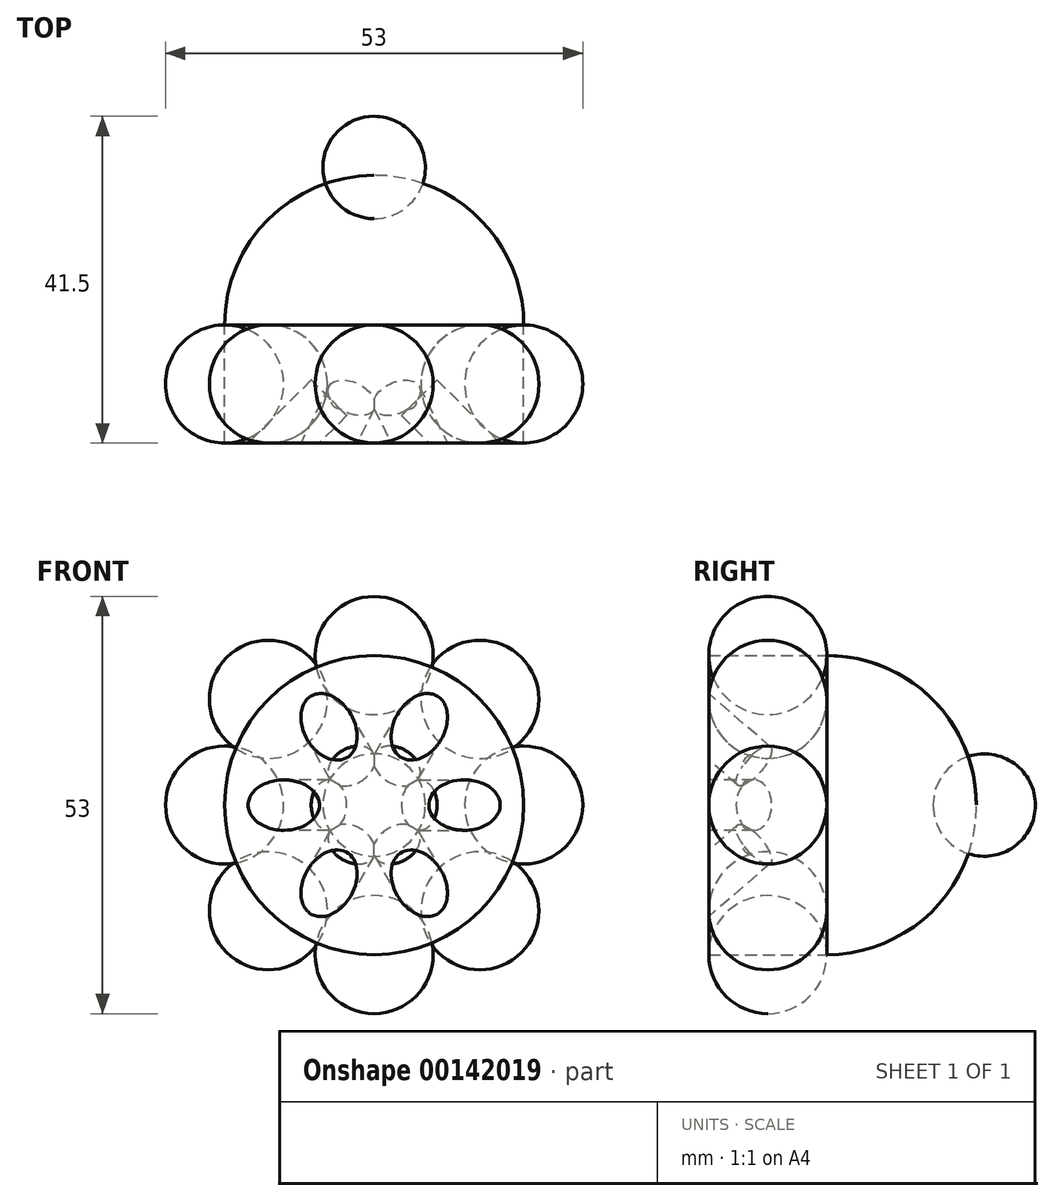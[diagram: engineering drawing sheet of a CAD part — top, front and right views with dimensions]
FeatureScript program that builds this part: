
annotation { "Feature Type Name" : "Feature", "Feature Type Description" : "" }
export const myFeature = defineFeature(function(context is Context, id is Id, definition is map)
    precondition{}
    {
        {
            var Q0;
            Q0=qCreatedBy(makeId("Front.planeOp"),FACE);
            var sketch = newSketch(context, id + "F0", { "sketchPlane" : qUnion([Q0])});
            skArc(sketch, "E0", {"start": v(7.5, 19) * mm, "mid": v(0, 26.5) * mm, "end": v(-7.5, 19) * mm});
            skLineSegment(sketch, "E1", {"start": v(-7.5, 19) * mm, "end": v(7.5, 19) * mm});
            skLineSegment(sketch, "E2", {"start": v(0, 19) * mm, "end": v(0, 0) * mm});
            skSolve(sketch);
        }
        {
            var Q0;
            Q0 = qSketchRegion(id + "F0", true);
            var Q1;
            Q1=sQuery(id+"F0.wireOp",EDGE,"E1");
            revolve(context, id + "F1", {"entities" : qUnion([Q0]), "axis" : qUnion([Q1]), "revolveType" : RevolveType.FULL});
        }
        {
            var Q0;
            Q0=qCreatedBy(makeId("Top.planeOp"),FACE);
            var sketch = newSketch(context, id + "F2", { "sketchPlane" : qUnion([Q0])});
            skLineSegment(sketch, "E3", {"start": v(0, 71.79) * mm, "end": v(0, -73.96) * mm});
            skSolve(sketch);
        }
        {
            var Q0;
            Q0=makeQuery(id+"F1.opRevolve","SWEPT_BODY",BODY,{"disambiguationData":[OSD([sQuery(id+"F0.wireOp",EDGE,"E0"),sQuery(id+"F0.wireOp",EDGE,"E1")])]});
            var Q1;
            Q1=sQuery(id+"F2.wireOp",EDGE,"E3");
            circularPattern(context, id + "F3", {"entities" : qUnion([Q0]), "axis" : qUnion([Q1]), "angle" : 45 * degree, "instanceCount" : 8});
        }
        {
            var Q0;
            Q0=qCreatedBy(makeId("Front.planeOp"),FACE);
            var sketch = newSketch(context, id + "F4", { "sketchPlane" : qUnion([Q0])});
            skCircle(sketch, "E4", {"center": v(0, 0) * mm, "radius": 19 * mm});
            skSolve(sketch);
        }
        {
            var Q0;
            Q0 = qSketchRegion(id + "F4", true);
            extrude(context, id + "F5", {"entities" : qUnion([Q0]), "endBound" : BoundingType.SYMMETRIC, "depth" : 15 * mm, "hasSecondDirection" : true, "secondDirectionOppositeDirection" : true, "secondDirectionDepth" : 25 * mm});
        }
        {
            var Q0;
            Q0=qCreatedBy(makeId("Right.planeOp"),FACE);
            var sketch = newSketch(context, id + "F6", { "sketchPlane" : qUnion([Q0])});
            skArc(sketch, "E5", {"start": v(26.5, 0) * mm, "mid": v(20.94, 13.44) * mm, "end": v(7.5, 19) * mm});
            skLineSegment(sketch, "E6", {"start": v(7.5, 19) * mm, "end": v(7.5, 0) * mm});
            skLineSegment(sketch, "E7", {"start": v(26.5, 0) * mm, "end": v(7.5, 0) * mm});
            skSolve(sketch);
        }
        {
            var Q0;
            Q0=qCreatedBy(makeId("Right.planeOp"),FACE);
            var sketch = newSketch(context, id + "F7", { "sketchPlane" : qUnion([Q0])});
            skLineSegment(sketch, "E8", {"start": v(118.27, 0) * mm, "end": v(-121.95, 0) * mm, "construction": true});
            skSolve(sketch);
        }
        {
            var Q0;
            Q0 = qSketchRegion(id + "F6", true);
            var Q1;
            Q1=sQuery(id+"F7.wireOp",EDGE,"E8");
            revolve(context, id + "F8", {"entities" : qUnion([Q0]), "axis" : qUnion([Q1]), "revolveType" : RevolveType.FULL});
        }
        {
            var Q0;
            Q0=qCreatedBy(makeId("Right.planeOp"),FACE);
            var sketch = newSketch(context, id + "F9", { "sketchPlane" : qUnion([Q0])});
            skArc(sketch, "E9", {"start": v(34, 0) * mm, "mid": v(27.5, 6.5) * mm, "end": v(21, 0) * mm});
            skLineSegment(sketch, "E10", {"start": v(34, 0) * mm, "end": v(21, 0) * mm});
            skSolve(sketch);
        }
        {
            var Q0;
            Q0=makeQuery(id+"F9.imprint","IMPRINT",FACE,{"disambiguationData":[TD([[makeQuery(id+"F9.imprint","IMPRINT",EDGE,{"derivedFrom":sQuery(id+"F9.wireOp",EDGE,"E9")}),1.0]])]});
            var Q1;
            Q1=sQuery(id+"F9.wireOp",EDGE,"E9");
            var Q2;
            Q2=sQuery(id+"F7.wireOp",EDGE,"E8");
            revolve(context, id + "F10", {"entities" : qUnion([Q0]), "surfaceEntities" : qUnion([Q1]), "axis" : qUnion([Q2]), "revolveType" : RevolveType.FULL});
        }
        {
            var Q0;
            Q0=qCreatedBy(makeId("Top.planeOp"),FACE);
            var sketch = newSketch(context, id + "F11", { "sketchPlane" : qUnion([Q0])});
            skLineSegment(sketch, "E11", {"start": v(-16, -7.5) * mm, "end": v(-8, 0.5) * mm});
            skLineSegment(sketch, "E12", {"start": v(0, -7.5) * mm, "end": v(-143.96, 136.46) * mm, "construction": true});
            skLineSegment(sketch, "E13", {"start": v(-65.01, -61.04) * mm, "end": v(127.86, 131.84) * mm, "construction": true});
            skLineSegment(sketch, "E14", {"start": v(-8, 0.5) * mm, "end": v(-5.74, -1.76) * mm});
            skLineSegment(sketch, "E15", {"start": v(-5.74, -1.76) * mm, "end": v(-11.47, -7.5) * mm});
            skLineSegment(sketch, "E16", {"start": v(-11.47, -7.5) * mm, "end": v(-16, -7.5) * mm});
            skSolve(sketch);
        }
        {
            var Q0;
            Q0 = qSketchRegion(id + "F11", true);
            var Q1;
            Q1=sQuery(id+"F11.wireOp",EDGE,"E13");
            revolve(context, id + "F12", {"entities" : qUnion([Q0]), "axis" : qUnion([Q1]), "revolveType" : RevolveType.FULL});
        }
        {
            var Q0;
            Q0=makeQuery(id+"F12.opRevolve","SWEPT_BODY",BODY,{"disambiguationData":[OSD([sQuery(id+"F11.wireOp",EDGE,"E11"),sQuery(id+"F11.wireOp",EDGE,"E15"),sQuery(id+"F11.wireOp",EDGE,"E16"),sQuery(id+"F11.wireOp",EDGE,"HOoqhNjA-D5fc-TMDI-aKYZ-cZDTuwgksI9U")])]});
            var Q1;
            Q1=sQuery(id+"F7.wireOp",EDGE,"E8");
            circularPattern(context, id + "F13", {"entities" : qUnion([Q0]), "axis" : qUnion([Q1]), "angle" : 60 * degree, "instanceCount" : 6});
        }
        {
            var Q0;
            Q0=makeQuery(id+"F13.opPattern","COPY",BODY,{"derivedFrom":makeQuery(id+"F12.opRevolve","SWEPT_BODY",BODY,{"disambiguationData":[OSD([sQuery(id+"F11.wireOp",EDGE,"E11"),sQuery(id+"F11.wireOp",EDGE,"E15"),sQuery(id+"F11.wireOp",EDGE,"E16"),sQuery(id+"F11.wireOp",EDGE,"HOoqhNjA-D5fc-TMDI-aKYZ-cZDTuwgksI9U")])]}),"instanceName":"3"});
            var Q1;
            Q1=makeQuery(id+"F12.opRevolve","SWEPT_BODY",BODY,{"disambiguationData":[OSD([sQuery(id+"F11.wireOp",EDGE,"E11"),sQuery(id+"F11.wireOp",EDGE,"E15"),sQuery(id+"F11.wireOp",EDGE,"E16"),sQuery(id+"F11.wireOp",EDGE,"HOoqhNjA-D5fc-TMDI-aKYZ-cZDTuwgksI9U")])]});
            var Q2;
            Q2=makeQuery(id+"F13.opPattern","COPY",BODY,{"derivedFrom":makeQuery(id+"F12.opRevolve","SWEPT_BODY",BODY,{"disambiguationData":[OSD([sQuery(id+"F11.wireOp",EDGE,"E11"),sQuery(id+"F11.wireOp",EDGE,"E15"),sQuery(id+"F11.wireOp",EDGE,"E16"),sQuery(id+"F11.wireOp",EDGE,"HOoqhNjA-D5fc-TMDI-aKYZ-cZDTuwgksI9U")])]}),"instanceName":"1"});
            var Q3;
            Q3=makeQuery(id+"F13.opPattern","COPY",BODY,{"derivedFrom":makeQuery(id+"F12.opRevolve","SWEPT_BODY",BODY,{"disambiguationData":[OSD([sQuery(id+"F11.wireOp",EDGE,"E11"),sQuery(id+"F11.wireOp",EDGE,"E15"),sQuery(id+"F11.wireOp",EDGE,"E16"),sQuery(id+"F11.wireOp",EDGE,"HOoqhNjA-D5fc-TMDI-aKYZ-cZDTuwgksI9U")])]}),"instanceName":"2"});
            var Q4;
            Q4=makeQuery(id+"F13.opPattern","COPY",BODY,{"derivedFrom":makeQuery(id+"F12.opRevolve","SWEPT_BODY",BODY,{"disambiguationData":[OSD([sQuery(id+"F11.wireOp",EDGE,"E11"),sQuery(id+"F11.wireOp",EDGE,"E14"),sQuery(id+"F11.wireOp",EDGE,"E15"),sQuery(id+"F11.wireOp",EDGE,"E16")])]}),"instanceName":"4"});
            var Q5;
            Q5=makeQuery(id+"F13.opPattern","COPY",BODY,{"derivedFrom":makeQuery(id+"F12.opRevolve","SWEPT_BODY",BODY,{"disambiguationData":[OSD([sQuery(id+"F11.wireOp",EDGE,"E11"),sQuery(id+"F11.wireOp",EDGE,"E14"),sQuery(id+"F11.wireOp",EDGE,"E15"),sQuery(id+"F11.wireOp",EDGE,"E16")])]}),"instanceName":"5"});
            var Q6;
            Q6=makeQuery(id+"F5.opExtrude","SWEPT_BODY",BODY,{"disambiguationData":[OSD([sQuery(id+"F4.wireOp",EDGE,"E4")])]});
            booleanBodies(context, id + "F14", {"operationType" : BooleanOperationType.SUBTRACTION, "tools" : qUnion([Q0, Q1, Q2, Q3, Q4, Q5]), "targets" : qUnion([Q6])});
        }
    });
